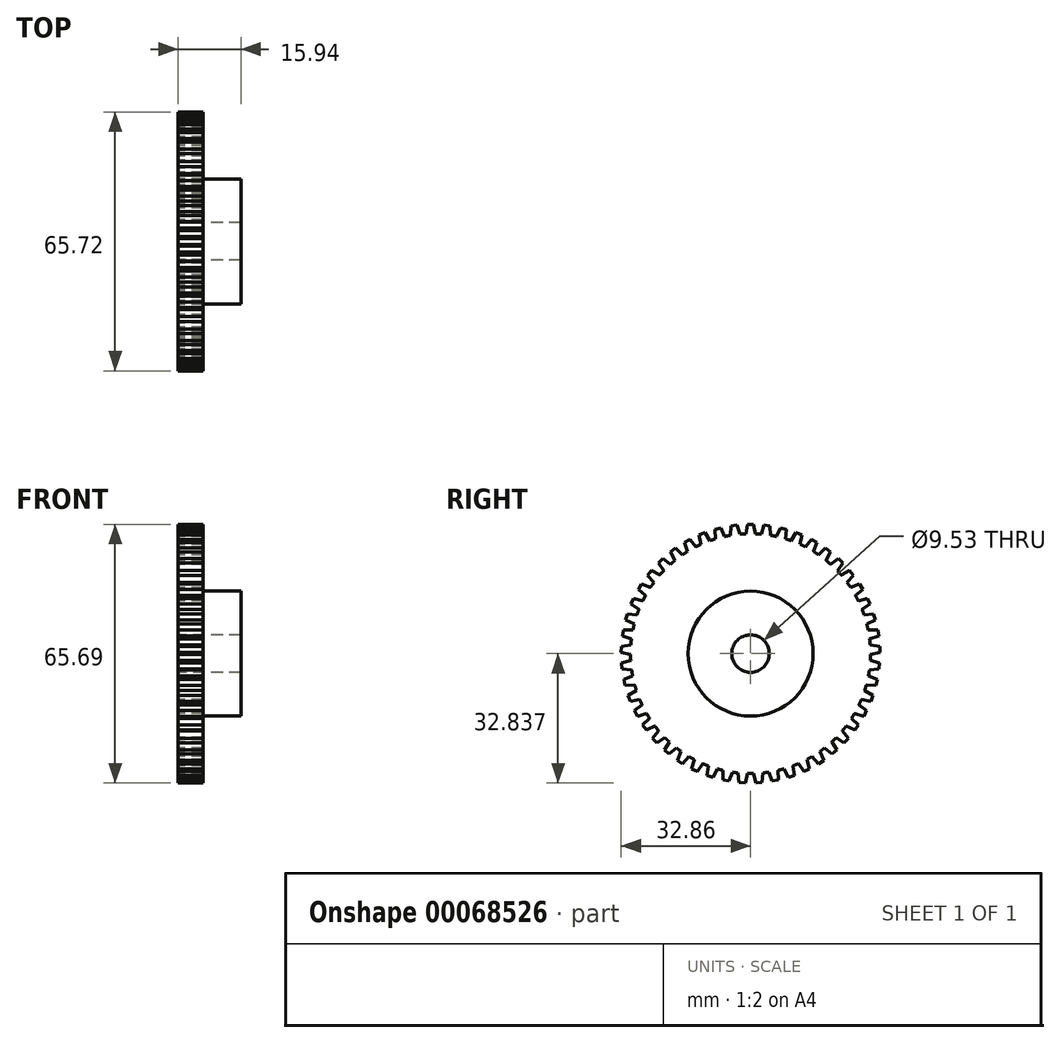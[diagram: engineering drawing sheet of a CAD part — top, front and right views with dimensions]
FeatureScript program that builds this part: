
annotation { "Feature Type Name" : "Feature", "Feature Type Description" : "" }
export const myFeature = defineFeature(function(context is Context, id is Id, definition is map)
    precondition{}
    {
        {
            var Q0;
            Q0=qCreatedBy(makeId("Front.planeOp"),FACE);
            var sketch = newSketch(context, id + "F0", { "sketchPlane" : qUnion([Q0])});
            skLineSegment(sketch, "E0", {"start": v(-9.59, 25.72) * mm, "end": v(-15.94, 25.72) * mm});
            skLineSegment(sketch, "E1", {"start": v(-15.94, 25.72) * mm, "end": v(-15.94, 0) * mm});
            skLineSegment(sketch, "E2", {"start": v(-15.94, 0) * mm, "end": v(0, 0) * mm});
            skLineSegment(sketch, "E3", {"start": v(0, 0) * mm, "end": v(0, 11.11) * mm});
            skLineSegment(sketch, "E4", {"start": v(0, 11.11) * mm, "end": v(-9.59, 11.11) * mm});
            skLineSegment(sketch, "E5", {"start": v(-9.59, 11.11) * mm, "end": v(-9.59, 25.72) * mm});
            skLineSegment(sketch, "E6", {"start": v(-36.23, -4.76) * mm, "end": v(27.64, -4.76) * mm, "construction": true});
            skSolve(sketch);
        }
        {
            var Q0;
            Q0=makeQuery(id+"F0.imprint","IMPRINT",FACE,{"disambiguationData":[TD([[makeQuery(id+"F0.imprint","IMPRINT",EDGE,{"derivedFrom":sQuery(id+"F0.wireOp",EDGE,"E0")}),1.0]])]});
            var Q1;
            Q1=sQuery(id+"F0.wireOp",EDGE,"E6");
            revolve(context, id + "F1", {"entities" : qUnion([Q0]), "axis" : qUnion([Q1]), "revolveType" : RevolveType.FULL});
        }
        {
            var Q0;
            Q0=qCreatedBy(makeId("Right.planeOp"),FACE);
            var sketch = newSketch(context, id + "F2", { "sketchPlane" : qUnion([Q0])});
            skLineSegment(sketch, "E7", {"start": v(0, 23.29) * mm, "end": v(0, 34.03) * mm, "construction": true});
            skLineSegment(sketch, "E8", {"start": v(0.8, 28.09) * mm, "end": v(1.2, 25.7) * mm});
            skLineSegment(sketch, "E9", {"start": v(0.8, 28.09) * mm, "end": v(0, 28.09) * mm});
            skLineSegment(sketch, "E10", {"start": v(1.2, 25.7) * mm, "end": v(0, 25.7) * mm});
            skCircle(sketch, "E11.0", {"center": v(0, -4.76) * mm, "radius": 30.48 * mm});
            skLineSegment(sketch, "E12.MirrorCS", {"start": v(-0.8, 28.09) * mm, "end": v(-1.2, 25.7) * mm});
            skLineSegment(sketch, "E13.MirrorCS", {"start": v(-0.8, 28.09) * mm, "end": v(0, 28.09) * mm});
            skSolve(sketch);
        }
        {
            var Q0;
            Q0=makeQuery(id+"F1.opRevolve","SWEPT_FACE",FACE,{"disambiguationData":[OSD([sQuery(id+"F0.wireOp",EDGE,"E1")])]});
            var sketch = newSketch(context, id + "F3", { "sketchPlane" : qUnion([Q0])});
            skCircle(sketch, "E14.0", {"center": v(0, -4.76) * mm, "radius": 30.48 * mm});
            skLineSegment(sketch, "E14.1", {"start": v(-0.8, 28.09) * mm, "end": v(-1.2, 25.7) * mm});
            skLineSegment(sketch, "E14.2", {"start": v(0.8, 28.09) * mm, "end": v(1.2, 25.7) * mm});
            skLineSegment(sketch, "E14.3", {"start": v(0.8, 28.09) * mm, "end": v(0, 28.09) * mm});
            skLineSegment(sketch, "E14.4", {"start": v(-0.8, 28.09) * mm, "end": v(0, 28.09) * mm});
            skSolve(sketch);
        }
        {
            var Q0;
            {var subQ1=sQuery(id+"F3.wireOp",EDGE,"E14.1");Q0=makeQuery(id+"F3.imprint","IMPRINT",FACE,{"disambiguationData":[TD([[makeQuery(id+"F3.imprint","IMPRINT",EDGE,{"derivedFrom":subQ1}),1.0]])]});}
            extrude(context, id + "F4", {"entities" : qUnion([Q0]), "operationType" : NewBodyOperationType.ADD, "oppositeDirection" : true, "depth" : 6.35 * mm});
        }
        {
            var Q0;
            Q0=makeQuery(id+"F1.opRevolve","SWEPT_BODY",BODY,{"disambiguationData":[OSD([sQuery(id+"F0.wireOp",EDGE,"E0"),sQuery(id+"F0.wireOp",EDGE,"E1"),sQuery(id+"F0.wireOp",EDGE,"E2"),sQuery(id+"F0.wireOp",EDGE,"E3"),sQuery(id+"F0.wireOp",EDGE,"E4"),sQuery(id+"F0.wireOp",EDGE,"E5")])]});
            var Q1;
            Q1=sQuery(id+"F3.wireOp",EDGE,"E14.0");
            circularPattern(context, id + "F5", {"operationType" : NewBodyOperationType.ADD, "entities" : qUnion([Q0]), "axis" : qUnion([Q1]), "angle" : 360 * degree, "instanceCount" : 49, "equalSpace" : true});
        }
    });
